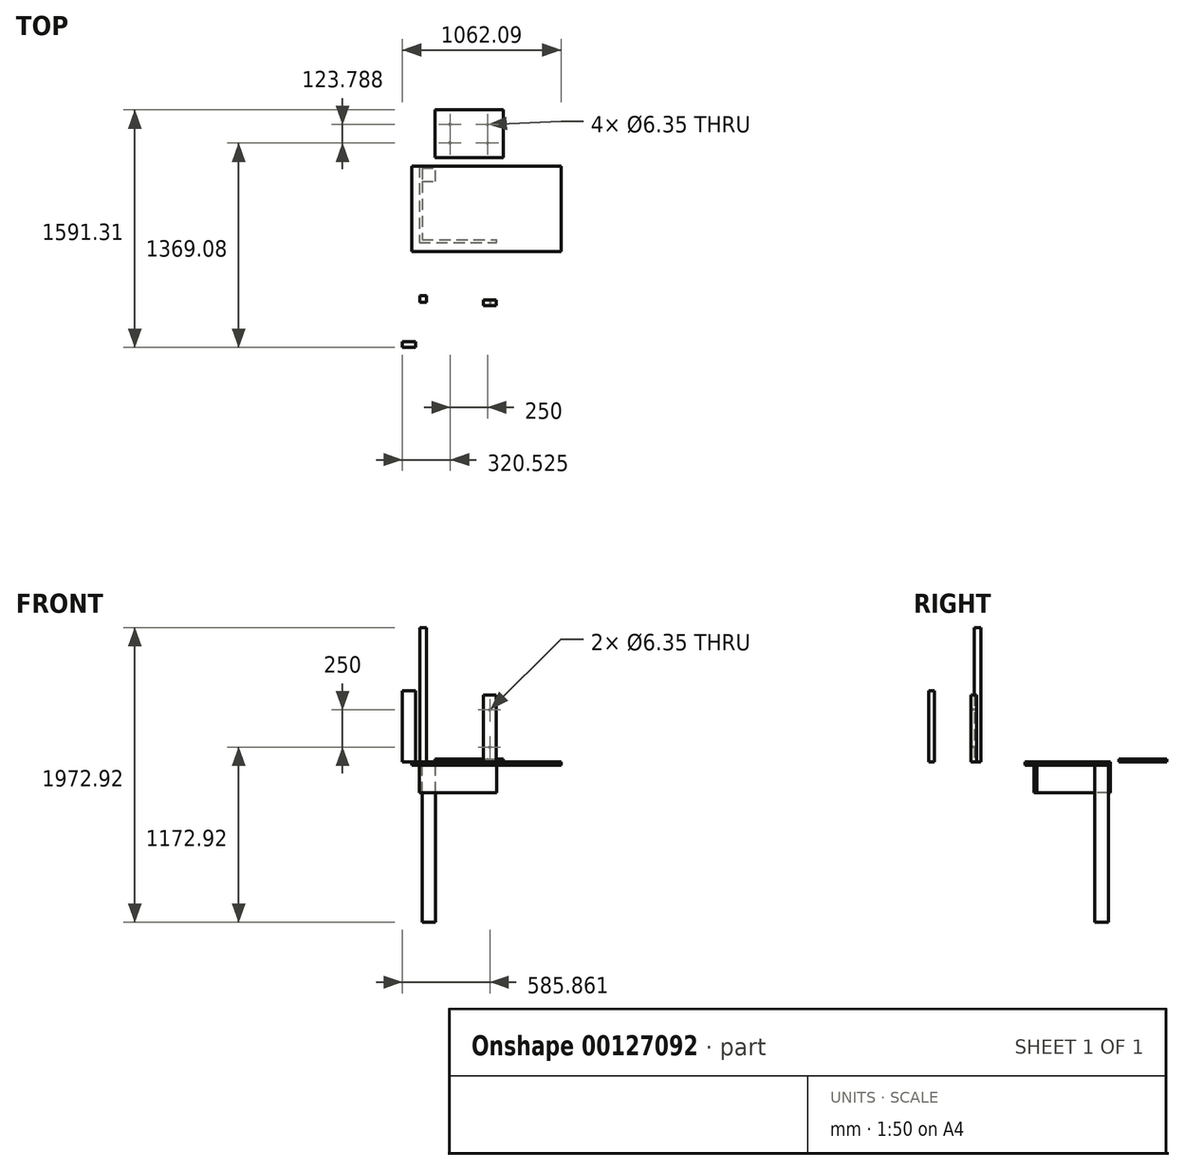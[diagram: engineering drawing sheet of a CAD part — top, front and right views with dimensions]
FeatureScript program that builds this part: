
annotation { "Feature Type Name" : "Feature", "Feature Type Description" : "" }
export const myFeature = defineFeature(function(context is Context, id is Id, definition is map)
    precondition{}
    {
        {
            var Q0;
            Q0=qCreatedBy(makeId("Top.planeOp"),FACE);
            var sketch = newSketch(context, id + "F0", { "sketchPlane" : qUnion([Q0])});
            skLineSegment(sketch, "E0.bottom", {"start": v(-324.21, 277.27) * mm, "end": v(132.99, 277.27) * mm});
            skLineSegment(sketch, "E0.top", {"start": v(-324.21, -43.4) * mm, "end": v(132.99, -43.4) * mm});
            skLineSegment(sketch, "E0.left", {"start": v(-324.21, 277.27) * mm, "end": v(-324.21, -43.4) * mm});
            skLineSegment(sketch, "E0.right", {"start": v(132.99, 277.27) * mm, "end": v(132.99, -43.4) * mm});
            skSolve(sketch);
        }
        {
            var Q0;
            Q0=makeQuery(id+"F0.imprint","IMPRINT",FACE,{"disambiguationData":[TD([[makeQuery(id+"F0.imprint","IMPRINT",EDGE,{"derivedFrom":sQuery(id+"F0.wireOp",EDGE,"E0.bottom")}),-1.0]])]});
            extrude(context, id + "F1", {"entities" : qUnion([Q0]), "depth" : 19.05 * mm});
        }
        {
            var Q0;
            Q0=qCreatedBy(makeId("Top.planeOp"),FACE);
            var sketch = newSketch(context, id + "F2", { "sketchPlane" : qUnion([Q0])});
            skLineSegment(sketch, "E1.bottom", {"start": v(-479.05, -100) * mm, "end": v(520.95, -100) * mm});
            skLineSegment(sketch, "E1.top", {"start": v(-479.05, -671.5) * mm, "end": v(520.95, -671.5) * mm});
            skLineSegment(sketch, "E1.left", {"start": v(-479.05, -100) * mm, "end": v(-479.05, -671.5) * mm});
            skLineSegment(sketch, "E1.right", {"start": v(520.95, -100) * mm, "end": v(520.95, -671.5) * mm});
            skSolve(sketch);
        }
        {
            var Q0;
            Q0=makeQuery(id+"F2.imprint","IMPRINT",FACE,{"disambiguationData":[TD([[makeQuery(id+"F2.imprint","IMPRINT",EDGE,{"derivedFrom":sQuery(id+"F2.wireOp",EDGE,"E1.bottom")}),-1.0]])]});
            extrude(context, id + "F3", {"entities" : qUnion([Q0]), "oppositeDirection" : true, "depth" : 22 * mm});
        }
        {
            var Q0;
            Q0=makeQuery(id+"F3.opExtrude","CAP_FACE",FACE,{"disambiguationData":[OSD([sQuery(id+"F2.wireOp",EDGE,"E1.bottom"),sQuery(id+"F2.wireOp",EDGE,"E1.top"),sQuery(id+"F2.wireOp",EDGE,"E1.left"),sQuery(id+"F2.wireOp",EDGE,"E1.right")])],"isStart":false});
            var sketch = newSketch(context, id + "F4", { "sketchPlane" : qUnion([Q0])});
            skLineSegment(sketch, "E2.bottom", {"start": v(-429.05, 100) * mm, "end": v(-409.05, 100) * mm});
            skLineSegment(sketch, "E2.top", {"start": v(-429.05, 611.5) * mm, "end": v(-409.05, 611.5) * mm});
            skLineSegment(sketch, "E2.left", {"start": v(-429.05, 100) * mm, "end": v(-429.05, 611.5) * mm});
            skLineSegment(sketch, "E2.right", {"start": v(-409.05, 100) * mm, "end": v(-409.05, 611.5) * mm});
            skPoint(sketch, "E2.middle", {"position": v(-419.05, 355.75) * mm});
            skLineSegment(sketch, "E3.bottom", {"start": v(-409.05, 611.5) * mm, "end": v(90.95, 611.5) * mm});
            skLineSegment(sketch, "E3.top", {"start": v(-409.05, 591.5) * mm, "end": v(90.95, 591.5) * mm});
            skLineSegment(sketch, "E3.left", {"start": v(-409.05, 611.5) * mm, "end": v(-409.05, 591.5) * mm});
            skLineSegment(sketch, "E3.right", {"start": v(90.95, 611.5) * mm, "end": v(90.95, 591.5) * mm});
            skLineSegment(sketch, "E4.left", {"start": v(-409.05, 100) * mm, "end": v(-409.05, 120) * mm});
            skLineSegment(sketch, "E5.bottom", {"start": v(-409.05, 591.5) * mm, "end": v(-320.05, 591.5) * mm});
            skLineSegment(sketch, "E5.top", {"start": v(-409.05, 502.5) * mm, "end": v(-320.05, 502.5) * mm});
            skLineSegment(sketch, "E5.left", {"start": v(-409.05, 591.5) * mm, "end": v(-409.05, 502.5) * mm});
            skLineSegment(sketch, "E5.right", {"start": v(-320.05, 591.5) * mm, "end": v(-320.05, 502.5) * mm});
            skLineSegment(sketch, "E6.bottom", {"start": v(-409.05, 202.5) * mm, "end": v(-320.05, 202.5) * mm});
            skLineSegment(sketch, "E6.top", {"start": v(-409.05, 113.5) * mm, "end": v(-320.05, 113.5) * mm});
            skLineSegment(sketch, "E6.left", {"start": v(-409.05, 202.5) * mm, "end": v(-409.05, 113.5) * mm});
            skLineSegment(sketch, "E6.right", {"start": v(-320.05, 202.5) * mm, "end": v(-320.05, 113.5) * mm});
            skSolve(sketch);
        }
        {
            var Q0;
            Q0=makeQuery(id+"F4.imprint","IMPRINT",FACE,{"disambiguationData":[TD([[makeQuery(id+"F4.imprint","IMPRINT",EDGE,{"derivedFrom":sQuery(id+"F4.wireOp",EDGE,"E3.bottom")}),-1.0]])]});
            var Q1;
            Q1=makeQuery(id+"F4.imprint","IMPRINT",FACE,{"disambiguationData":[TD([[makeQuery(id+"F4.imprint","IMPRINT",EDGE,{"derivedFrom":sQuery(id+"F4.wireOp",EDGE,"E2.bottom")}),1.0]])]});
            var Q2;
            Q2=makeQuery(id+"F4.imprint","IMPRINT",FACE,{"disambiguationData":[TD([[makeQuery(id+"F4.imprint","IMPRINT",EDGE,{"derivedFrom":sQuery(id+"F4.wireOp",EDGE,"E4.bottom")}),1.0]])]});
            extrude(context, id + "F5", {"entities" : qUnion([Q0, Q1, Q2]), "operationType" : NewBodyOperationType.ADD, "depth" : 184 * mm});
        }
        {
            var Q0;
            Q0=makeQuery(id+"F4.imprint","IMPRINT",FACE,{"disambiguationData":[TD([[makeQuery(id+"F4.imprint","IMPRINT",EDGE,{"derivedFrom":sQuery(id+"F4.wireOp",EDGE,"E5.bottom")}),-1.0]])]});
            var Q1;
            {var subQ3=sQuery(id+"F4.wireOp",EDGE,"E6.bottom");Q1=makeQuery(id+"F4.imprint","IMPRINT",FACE,{"disambiguationData":[TD([[makeQuery(id+"F4.imprint","IMPRINT",EDGE,{"derivedFrom":subQ3}),-1.0]])]});}
            extrude(context, id + "F6", {"entities" : qUnion([Q0, Q1]), "operationType" : NewBodyOperationType.ADD, "depth" : 1050.92 * mm});
        }
        {
            var Q0;
            Q0=qCreatedBy(makeId("Top.planeOp"),FACE);
            var sketch = newSketch(context, id + "F7", { "sketchPlane" : qUnion([Q0])});
            skLineSegment(sketch, "E7.bottom", {"start": v(-425.84, -966.9) * mm, "end": v(-381.39, -966.9) * mm});
            skLineSegment(sketch, "E7.top", {"start": v(-425.84, -1011.34) * mm, "end": v(-381.39, -1011.34) * mm});
            skLineSegment(sketch, "E7.left", {"start": v(-425.84, -966.9) * mm, "end": v(-425.84, -1011.34) * mm});
            skLineSegment(sketch, "E7.right", {"start": v(-381.39, -966.9) * mm, "end": v(-381.39, -1011.34) * mm});
            skSolve(sketch);
        }
        {
            var Q0;
            Q0=makeQuery(id+"F7.imprint","IMPRINT",FACE,{"disambiguationData":[TD([[makeQuery(id+"F7.imprint","IMPRINT",EDGE,{"derivedFrom":sQuery(id+"F7.wireOp",EDGE,"E7.bottom")}),-1.0]])]});
            extrude(context, id + "F8", {"entities" : qUnion([Q0]), "depth" : 900 * mm});
        }
        {
            var Q0;
            Q0=qCreatedBy(makeId("Top.planeOp"),FACE);
            var sketch = newSketch(context, id + "F9", { "sketchPlane" : qUnion([Q0])});
            skLineSegment(sketch, "E8.bottom", {"start": v(88.38, -996.08) * mm, "end": v(1.06, -996.08) * mm});
            skLineSegment(sketch, "E8.top", {"start": v(88.38, -1034.18) * mm, "end": v(1.06, -1034.18) * mm});
            skLineSegment(sketch, "E8.left", {"start": v(88.38, -996.08) * mm, "end": v(88.38, -1034.18) * mm});
            skLineSegment(sketch, "E8.right", {"start": v(1.06, -996.08) * mm, "end": v(1.06, -1034.18) * mm});
            skSolve(sketch);
        }
        {
            var Q0;
            Q0 = qSketchRegion(id + "F9", true);
            extrude(context, id + "F10", {"entities" : qUnion([Q0]), "depth" : 450 * mm});
        }
        {
            var Q0;
            Q0=makeQuery(id+"F1.opExtrude","CAP_FACE",FACE,{"disambiguationData":[OSD([sQuery(id+"F0.wireOp",EDGE,"E0.bottom"),sQuery(id+"F0.wireOp",EDGE,"E0.top"),sQuery(id+"F0.wireOp",EDGE,"E0.left"),sQuery(id+"F0.wireOp",EDGE,"E0.right")])],"isStart":false});
            var sketch = newSketch(context, id + "F11", { "sketchPlane" : qUnion([Q0])});
            skCircle(sketch, "E9", {"center": v(29.39, 55.03) * mm, "radius": 3.17 * mm});
            skCircle(sketch, "E10", {"center": v(29.39, 178.82) * mm, "radius": 3.17 * mm});
            skCircle(sketch, "E11", {"center": v(-220.61, 55.03) * mm, "radius": 3.17 * mm});
            skCircle(sketch, "E12", {"center": v(-220.61, 178.82) * mm, "radius": 3.17 * mm});
            skLineSegment(sketch, "E13", {"start": v(29.39, 55.03) * mm, "end": v(-220.61, 178.82) * mm, "construction": true});
            skPoint(sketch, "E14", {"position": v(-95.61, 116.93) * mm});
            skLineSegment(sketch, "E15", {"start": v(132.99, -43.4) * mm, "end": v(-324.21, 277.27) * mm, "construction": true});
            skSolve(sketch);
        }
        {
            var Q0;
            Q0 = qSketchRegion(id + "F11", true);
            extrude(context, id + "F12", {"entities" : qUnion([Q0]), "operationType" : NewBodyOperationType.REMOVE, "endBound" : BoundingType.UP_TO_NEXT, "oppositeDirection" : true, "depth" : 25 * mm});
        }
        {
            var Q0;
            Q0=makeQuery(id+"F10.opExtrude","SWEPT_FACE",FACE,{"disambiguationData":[OSD([sQuery(id+"F9.wireOp",EDGE,"E8.top")])]});
            var sketch = newSketch(context, id + "F13", { "sketchPlane" : qUnion([Q0])});
            skCircle(sketch, "E16", {"center": v(44.72, 350) * mm, "radius": 3.17 * mm});
            skCircle(sketch, "E17", {"center": v(44.72, 100) * mm, "radius": 3.17 * mm});
            skLineSegment(sketch, "E18", {"start": v(44.72, 350) * mm, "end": v(44.72, 100) * mm, "construction": true});
            skPoint(sketch, "E19", {"position": v(44.72, 225) * mm});
            skLineSegment(sketch, "E20", {"start": v(88.38, 450) * mm, "end": v(1.06, 0) * mm, "construction": true});
            skSolve(sketch);
        }
        {
            var Q0;
            Q0 = qSketchRegion(id + "F13", true);
            extrude(context, id + "F14", {"entities" : qUnion([Q0]), "operationType" : NewBodyOperationType.REMOVE, "endBound" : BoundingType.UP_TO_NEXT, "oppositeDirection" : true, "depth" : 25 * mm});
        }
        {
            var Q0;
            Q0=qCreatedBy(makeId("Top.planeOp"),FACE);
            var sketch = newSketch(context, id + "F15", { "sketchPlane" : qUnion([Q0])});
            skLineSegment(sketch, "E21.bottom", {"start": v(-541.14, -1275.94) * mm, "end": v(-452.24, -1275.94) * mm});
            skLineSegment(sketch, "E21.top", {"start": v(-541.14, -1314.04) * mm, "end": v(-452.24, -1314.04) * mm});
            skLineSegment(sketch, "E21.left", {"start": v(-541.14, -1275.94) * mm, "end": v(-541.14, -1314.04) * mm});
            skLineSegment(sketch, "E21.right", {"start": v(-452.24, -1275.94) * mm, "end": v(-452.24, -1314.04) * mm});
            skSolve(sketch);
        }
        {
            var Q0;
            Q0 = qSketchRegion(id + "F15", true);
            extrude(context, id + "F16", {"entities" : qUnion([Q0]), "depth" : 478 * mm});
        }
    });
